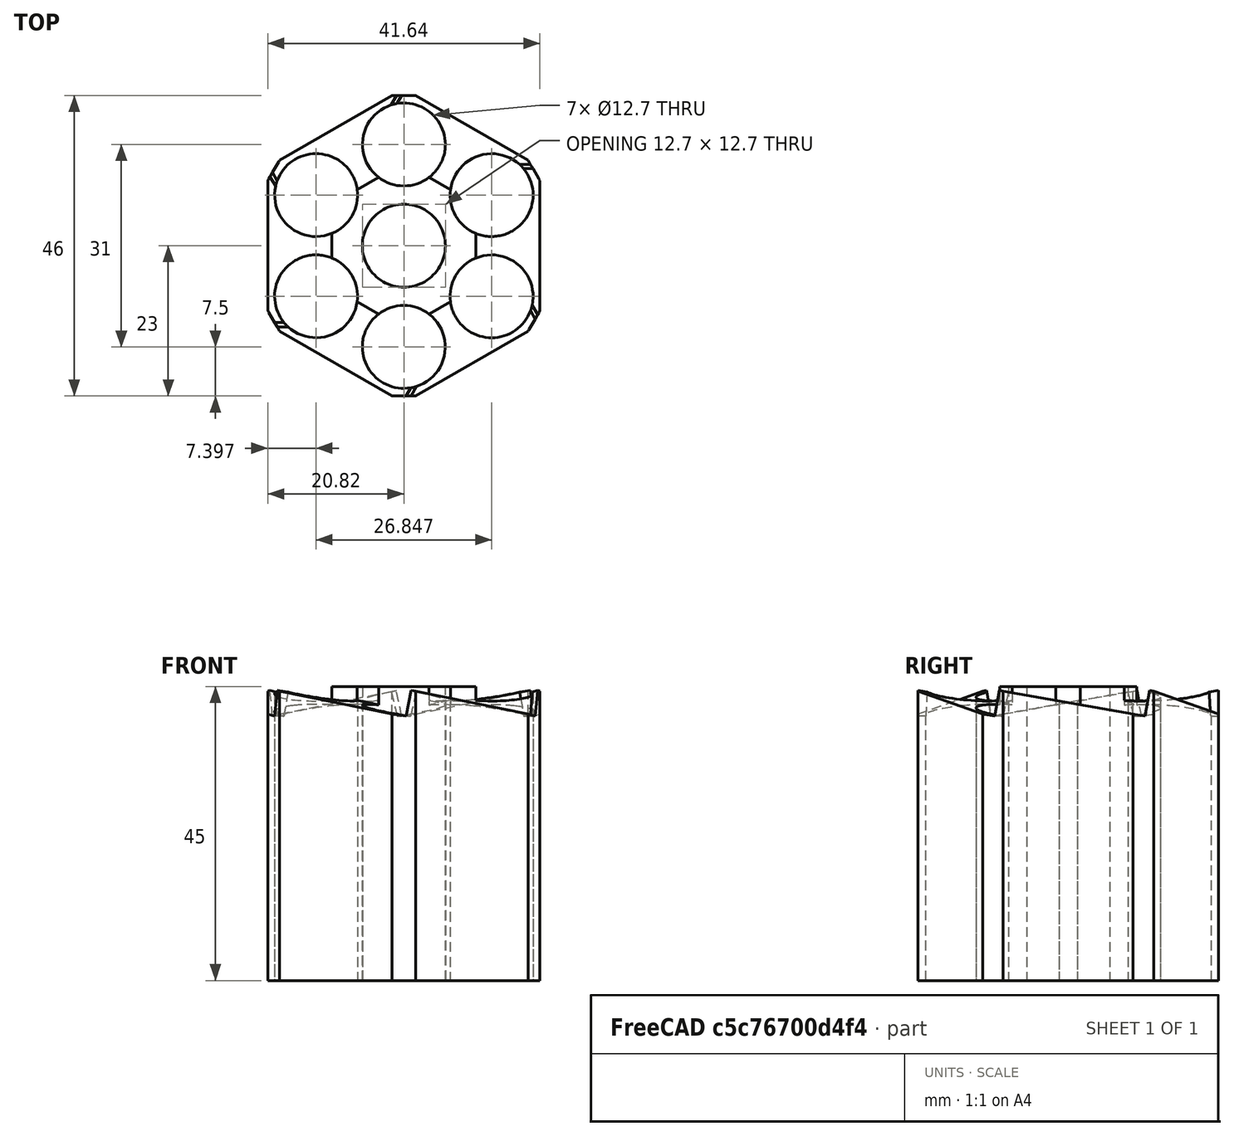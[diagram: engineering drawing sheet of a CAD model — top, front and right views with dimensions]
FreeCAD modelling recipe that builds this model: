
FCSTD DOCUMENT  (FreeCAD 0.20R29410 (Git))
Label: cylinderCore7
License: All rights reserved
LicenseURL: http://en.wikipedia.org/wiki/All_rights_reserved
objects: Part::MultiFuse×108, Part::Box×66, Part::Cylinder×51, Part::Cut×8, Part::Feature×1
note: 234 computed .brp shape members not serialized (recipe doc carries the construction recipe); baked Part::Feature solids carry a one-line shape summary decoded from their .brp

FEATURE [Part::Cylinder] Cylinder
  Angle = 360
  AttacherType = Attacher::AttachEngine3D
  FirstAngle = 0
  Height = 45
  Radius = 25
  SecondAngle = 0
FEATURE [Part::Cylinder] Cylinder001
  Angle = 360
  AttacherType = Attacher::AttachEngine3D
  FirstAngle = 0
  Height = 50
  Placement = pos=(0,15.5,0) rot=(0,0,1;0rad)
  Radius = 6.35
  SecondAngle = 0
FEATURE [Part::Cylinder] Cylinder002
  Angle = 360
  AttacherType = Attacher::AttachEngine3D
  FirstAngle = 0
  Height = 50
  Radius = 6.35
  SecondAngle = 0
FEATURE [Part::Cylinder] Cylinder003  label="bevilPin"
  Angle = 360
  AttacherType = Attacher::AttachEngine3D
  FirstAngle = 0
  Height = 55
  Radius = 6.35
  SecondAngle = 0
FEATURE [Part::MultiFuse] Fusion
  Shapes = -> [Cylinder001,Cylinder002]
FEATURE [Part::Box] Box  label="Cube"
  AttacherType = Attacher::AttachEngine3D
  Height = 50
  Length = 3
  Placement = pos=(-1.5,23,0) rot=(0,0,1;0rad)
  Width = 10
FEATURE [Part::Box] Box001  label="Cube001"
  AttacherType = Attacher::AttachEngine3D
  Height = 50
  Length = 3
  Placement = pos=(12.5753,23,-0.369646) rot=(0,-1,0;0.261799rad)
  Width = 10
FEATURE [Part::Box] Box002  label="Cube002"
  AttacherType = Attacher::AttachEngine3D
  Height = 50
  Length = 3
  Placement = pos=(-1.5,23,0) rot=(0,-1,0;0.523599rad)
  Width = 10
FEATURE [Part::MultiFuse] Fusion001
  Shapes = -> [Box,Box001]
FEATURE [Part::MultiFuse] Fusion002
  Shapes = -> [Fusion001,Box002]
FEATURE [Part::MultiFuse] Fusion003
  Shapes = -> [Fusion,Fusion002]
FEATURE [Part::Box] Box003  label="Cube003"
  AttacherType = Attacher::AttachEngine3D
  Height = 50
  Length = 3
  Placement = pos=(-1.5,23,0) rot=(0,0,1;0rad)
  Width = 10
FEATURE [Part::Box] Box004  label="Cube004"
  AttacherType = Attacher::AttachEngine3D
  Height = 50
  Length = 3
  Placement = pos=(12.5753,23,-0.369646) rot=(0,-1,0;0.261799rad)
  Width = 10
FEATURE [Part::Box] Box005  label="Cube005"
  AttacherType = Attacher::AttachEngine3D
  Height = 50
  Length = 3
  Placement = pos=(-1.5,23,0) rot=(0,-1,0;0.523599rad)
  Width = 10
FEATURE [Part::Cylinder] Cylinder004
  Angle = 360
  AttacherType = Attacher::AttachEngine3D
  FirstAngle = 0
  Height = 50
  Placement = pos=(0,15.5,0) rot=(0,0,1;0rad)
  Radius = 6.35
  SecondAngle = 0
FEATURE [Part::Cylinder] Cylinder005
  Angle = 360
  AttacherType = Attacher::AttachEngine3D
  FirstAngle = 0
  Height = 50
  Radius = 6.35
  SecondAngle = 0
FEATURE [Part::MultiFuse] Fusion004
  Shapes = -> [Cylinder004,Cylinder005]
FEATURE [Part::MultiFuse] Fusion005
  Shapes = -> [Box003,Box004]
FEATURE [Part::MultiFuse] Fusion006
  Shapes = -> [Fusion005,Box005]
FEATURE [Part::MultiFuse] Fusion007
  Placement = pos=(0,0,0) rot=(0,0,1;3.14159rad)
  Shapes = -> [Fusion004,Fusion006]
FEATURE [Part::MultiFuse] Fusion008
  Shapes = -> [Fusion007,Fusion003]
FEATURE [Part::Box] Box006  label="Cube006"
  AttacherType = Attacher::AttachEngine3D
  Height = 50
  Length = 3
  Placement = pos=(-1.5,23,0) rot=(0,0,1;0rad)
  Width = 10
FEATURE [Part::Box] Box007  label="Cube007"
  AttacherType = Attacher::AttachEngine3D
  Height = 50
  Length = 3
  Placement = pos=(12.5753,23,-0.369646) rot=(0,-1,0;0.261799rad)
  Width = 10
FEATURE [Part::Box] Box008  label="Cube008"
  AttacherType = Attacher::AttachEngine3D
  Height = 50
  Length = 3
  Placement = pos=(-1.5,23,0) rot=(0,-1,0;0.523599rad)
  Width = 10
FEATURE [Part::Box] Box009  label="Cube009"
  AttacherType = Attacher::AttachEngine3D
  Height = 50
  Length = 3
  Placement = pos=(-1.5,23,0) rot=(0,0,1;0rad)
  Width = 10
FEATURE [Part::Box] Box010  label="Cube010"
  AttacherType = Attacher::AttachEngine3D
  Height = 50
  Length = 3
  Placement = pos=(12.5753,23,-0.369646) rot=(0,-1,0;0.261799rad)
  Width = 10
FEATURE [Part::Box] Box011  label="Cube011"
  AttacherType = Attacher::AttachEngine3D
  Height = 50
  Length = 3
  Placement = pos=(-1.5,23,0) rot=(0,-1,0;0.523599rad)
  Width = 10
FEATURE [Part::Cylinder] Cylinder006
  Angle = 360
  AttacherType = Attacher::AttachEngine3D
  FirstAngle = 0
  Height = 50
  Placement = pos=(0,15.5,0) rot=(0,0,1;0rad)
  Radius = 6.35
  SecondAngle = 0
FEATURE [Part::Cylinder] Cylinder007
  Angle = 360
  AttacherType = Attacher::AttachEngine3D
  FirstAngle = 0
  Height = 50
  Radius = 6.35
  SecondAngle = 0
FEATURE [Part::Cylinder] Cylinder008
  Angle = 360
  AttacherType = Attacher::AttachEngine3D
  FirstAngle = 0
  Height = 50
  Placement = pos=(0,15.5,0) rot=(0,0,1;0rad)
  Radius = 6.35
  SecondAngle = 0
FEATURE [Part::Cylinder] Cylinder009
  Angle = 360
  AttacherType = Attacher::AttachEngine3D
  FirstAngle = 0
  Height = 50
  Radius = 6.35
  SecondAngle = 0
FEATURE [Part::MultiFuse] Fusion009
  Shapes = -> [Cylinder006,Cylinder007]
FEATURE [Part::MultiFuse] Fusion010
  Shapes = -> [Box006,Box007]
FEATURE [Part::MultiFuse] Fusion011
  Shapes = -> [Fusion010,Box008]
FEATURE [Part::MultiFuse] Fusion012
  Shapes = -> [Fusion009,Fusion011]
FEATURE [Part::MultiFuse] Fusion013
  Shapes = -> [Cylinder008,Cylinder009]
FEATURE [Part::MultiFuse] Fusion014
  Shapes = -> [Box009,Box010]
FEATURE [Part::MultiFuse] Fusion015
  Shapes = -> [Fusion014,Box011]
FEATURE [Part::MultiFuse] Fusion016
  Placement = pos=(0,0,0) rot=(0,0,1;3.14159rad)
  Shapes = -> [Fusion013,Fusion015]
FEATURE [Part::MultiFuse] Fusion017
  Placement = pos=(0,0,0) rot=(0,0,-1;1.0472rad)
  Shapes = -> [Fusion016,Fusion012]
FEATURE [Part::Box] Box012  label="Cube012"
  AttacherType = Attacher::AttachEngine3D
  Height = 50
  Length = 3
  Placement = pos=(-1.5,23,0) rot=(0,0,1;0rad)
  Width = 10
FEATURE [Part::Box] Box013  label="Cube013"
  AttacherType = Attacher::AttachEngine3D
  Height = 50
  Length = 3
  Placement = pos=(12.5753,23,-0.369646) rot=(0,-1,0;0.261799rad)
  Width = 10
FEATURE [Part::Box] Box014  label="Cube014"
  AttacherType = Attacher::AttachEngine3D
  Height = 50
  Length = 3
  Placement = pos=(-1.5,23,0) rot=(0,-1,0;0.523599rad)
  Width = 10
FEATURE [Part::Box] Box015  label="Cube015"
  AttacherType = Attacher::AttachEngine3D
  Height = 50
  Length = 3
  Placement = pos=(-1.5,23,0) rot=(0,0,1;0rad)
  Width = 10
FEATURE [Part::Box] Box016  label="Cube016"
  AttacherType = Attacher::AttachEngine3D
  Height = 50
  Length = 3
  Placement = pos=(12.5753,23,-0.369646) rot=(0,-1,0;0.261799rad)
  Width = 10
FEATURE [Part::Box] Box017  label="Cube017"
  AttacherType = Attacher::AttachEngine3D
  Height = 50
  Length = 3
  Placement = pos=(-1.5,23,0) rot=(0,-1,0;0.523599rad)
  Width = 10
FEATURE [Part::Cylinder] Cylinder010
  Angle = 360
  AttacherType = Attacher::AttachEngine3D
  FirstAngle = 0
  Height = 50
  Placement = pos=(0,15.5,0) rot=(0,0,1;0rad)
  Radius = 6.35
  SecondAngle = 0
FEATURE [Part::Cylinder] Cylinder011
  Angle = 360
  AttacherType = Attacher::AttachEngine3D
  FirstAngle = 0
  Height = 50
  Radius = 6.35
  SecondAngle = 0
FEATURE [Part::Cylinder] Cylinder012
  Angle = 360
  AttacherType = Attacher::AttachEngine3D
  FirstAngle = 0
  Height = 50
  Placement = pos=(0,15.5,0) rot=(0,0,1;0rad)
  Radius = 6.35
  SecondAngle = 0
FEATURE [Part::Cylinder] Cylinder013
  Angle = 360
  AttacherType = Attacher::AttachEngine3D
  FirstAngle = 0
  Height = 50
  Radius = 6.35
  SecondAngle = 0
FEATURE [Part::MultiFuse] Fusion018
  Shapes = -> [Cylinder010,Cylinder011]
FEATURE [Part::MultiFuse] Fusion019
  Shapes = -> [Box012,Box013]
FEATURE [Part::MultiFuse] Fusion020
  Shapes = -> [Fusion019,Box014]
FEATURE [Part::MultiFuse] Fusion021
  Shapes = -> [Fusion018,Fusion020]
FEATURE [Part::MultiFuse] Fusion022
  Shapes = -> [Cylinder012,Cylinder013]
FEATURE [Part::MultiFuse] Fusion023
  Shapes = -> [Box015,Box016]
FEATURE [Part::MultiFuse] Fusion024
  Shapes = -> [Fusion023,Box017]
FEATURE [Part::MultiFuse] Fusion025
  Placement = pos=(0,0,0) rot=(0,0,1;3.14159rad)
  Shapes = -> [Fusion022,Fusion024]
FEATURE [Part::MultiFuse] Fusion026
  Placement = pos=(0,0,0) rot=(0,0,1;4.18879rad)
  Shapes = -> [Fusion025,Fusion021]
FEATURE [Part::MultiFuse] Fusion027
  Shapes = -> [Fusion026,Fusion017]
FEATURE [Part::MultiFuse] Fusion028
  Shapes = -> [Fusion027,Fusion008]
FEATURE [Part::Cut] Cut
  Base = -> Cylinder
  Tool = -> Fusion028
FEATURE [Part::Box] Box018  label="Cube018"
  AttacherType = Attacher::AttachEngine3D
  Height = 50
  Length = 5
  Placement = pos=(-2.5,23,0) rot=(0,0,1;0rad)
  Width = 10
FEATURE [Part::Box] Box019  label="Cube019"
  AttacherType = Attacher::AttachEngine3D
  Height = 55
  Length = 5
  Placement = pos=(-1.23811,24.2566,-4.69879) rot=(0.041494,-0.428539,0.90257;0.912584rad)
  Width = 10
FEATURE [Part::Box] Box020  label="Cube020"
  AttacherType = Attacher::AttachEngine3D
  Height = 10
  Length = 7
  Placement = pos=(-4.5,23,0) rot=(0,0,1;0rad)
  Width = 10
FEATURE [Part::MultiFuse] Fusion029
  Shapes = -> [Box020,Box019]
FEATURE [Part::MultiFuse] Fusion030
  Shapes = -> [Fusion029,Box018]
FEATURE [Part::Cylinder] Cylinder014  label="bevilPin001"
  Angle = 360
  AttacherType = Attacher::AttachEngine3D
  FirstAngle = 0
  Height = 50
  Radius = 6.35
  SecondAngle = 0
FEATURE [Part::MultiFuse] Fusion031
  Shapes = -> [Cylinder014,Fusion030]
FEATURE [Part::Box] Box021  label="Cube021"
  AttacherType = Attacher::AttachEngine3D
  Height = 50
  Length = 5
  Placement = pos=(-2.5,23,0) rot=(0,0,1;0rad)
  Width = 10
FEATURE [Part::Box] Box022  label="Cube022"
  AttacherType = Attacher::AttachEngine3D
  Height = 55
  Length = 5
  Placement = pos=(-1.23811,24.2566,-4.69879) rot=(0.041494,-0.428539,0.90257;0.912584rad)
  Width = 10
FEATURE [Part::Box] Box023  label="Cube023"
  AttacherType = Attacher::AttachEngine3D
  Height = 10
  Length = 7
  Placement = pos=(-4.5,23,0) rot=(0,0,1;0rad)
  Width = 10
FEATURE [Part::Cylinder] Cylinder015  label="bevilPin002"
  Angle = 360
  AttacherType = Attacher::AttachEngine3D
  FirstAngle = 0
  Height = 50
  Radius = 6.35
  SecondAngle = 0
FEATURE [Part::MultiFuse] Fusion032
  Shapes = -> [Box023,Box022]
FEATURE [Part::MultiFuse] Fusion033
  Shapes = -> [Fusion032,Box021]
FEATURE [Part::MultiFuse] Fusion034
  Placement = pos=(0,0,0) rot=(0,0,1;3.14159rad)
  Shapes = -> [Cylinder015,Fusion033]
FEATURE [Part::MultiFuse] Fusion035
  Shapes = -> [Fusion034,Fusion031]
FEATURE [Part::Box] Box024  label="Cube024"
  AttacherType = Attacher::AttachEngine3D
  Height = 50
  Length = 5
  Placement = pos=(-2.5,23,0) rot=(0,0,1;0rad)
  Width = 10
FEATURE [Part::Box] Box025  label="Cube025"
  AttacherType = Attacher::AttachEngine3D
  Height = 55
  Length = 5
  Placement = pos=(-1.23811,24.2566,-4.69879) rot=(0.041494,-0.428539,0.90257;0.912584rad)
  Width = 10
FEATURE [Part::Box] Box026  label="Cube026"
  AttacherType = Attacher::AttachEngine3D
  Height = 10
  Length = 7
  Placement = pos=(-4.5,23,0) rot=(0,0,1;0rad)
  Width = 10
FEATURE [Part::Box] Box027  label="Cube027"
  AttacherType = Attacher::AttachEngine3D
  Height = 50
  Length = 5
  Placement = pos=(-2.5,23,0) rot=(0,0,1;0rad)
  Width = 10
FEATURE [Part::Box] Box028  label="Cube028"
  AttacherType = Attacher::AttachEngine3D
  Height = 55
  Length = 5
  Placement = pos=(-1.23811,24.2566,-4.69879) rot=(0.041494,-0.428539,0.90257;0.912584rad)
  Width = 10
FEATURE [Part::Box] Box029  label="Cube029"
  AttacherType = Attacher::AttachEngine3D
  Height = 10
  Length = 7
  Placement = pos=(-4.5,23,0) rot=(0,0,1;0rad)
  Width = 10
FEATURE [Part::Cylinder] Cylinder016  label="bevilPin003"
  Angle = 360
  AttacherType = Attacher::AttachEngine3D
  FirstAngle = 0
  Height = 50
  Radius = 6.35
  SecondAngle = 0
FEATURE [Part::Cylinder] Cylinder017  label="bevilPin004"
  Angle = 360
  AttacherType = Attacher::AttachEngine3D
  FirstAngle = 0
  Height = 50
  Radius = 6.35
  SecondAngle = 0
FEATURE [Part::MultiFuse] Fusion036
  Shapes = -> [Box026,Box025]
FEATURE [Part::MultiFuse] Fusion037
  Shapes = -> [Fusion036,Box024]
FEATURE [Part::MultiFuse] Fusion038
  Shapes = -> [Cylinder016,Fusion037]
FEATURE [Part::MultiFuse] Fusion039
  Shapes = -> [Box029,Box028]
FEATURE [Part::MultiFuse] Fusion040
  Shapes = -> [Fusion039,Box027]
FEATURE [Part::MultiFuse] Fusion041
  Placement = pos=(0,0,0) rot=(0,0,1;3.14159rad)
  Shapes = -> [Cylinder017,Fusion040]
FEATURE [Part::MultiFuse] Fusion042
  Placement = pos=(0,0,0) rot=(0,0,-1;1.0472rad)
  Shapes = -> [Fusion041,Fusion038]
FEATURE [Part::Box] Box030  label="Cube030"
  AttacherType = Attacher::AttachEngine3D
  Height = 50
  Length = 5
  Placement = pos=(-2.5,23,0) rot=(0,0,1;0rad)
  Width = 10
FEATURE [Part::Box] Box031  label="Cube031"
  AttacherType = Attacher::AttachEngine3D
  Height = 55
  Length = 5
  Placement = pos=(-1.23811,24.2566,-4.69879) rot=(0.041494,-0.428539,0.90257;0.912584rad)
  Width = 10
FEATURE [Part::Box] Box032  label="Cube032"
  AttacherType = Attacher::AttachEngine3D
  Height = 10
  Length = 7
  Placement = pos=(-4.5,23,0) rot=(0,0,1;0rad)
  Width = 10
FEATURE [Part::Box] Box033  label="Cube033"
  AttacherType = Attacher::AttachEngine3D
  Height = 50
  Length = 5
  Placement = pos=(-2.5,23,0) rot=(0,0,1;0rad)
  Width = 10
FEATURE [Part::Box] Box034  label="Cube034"
  AttacherType = Attacher::AttachEngine3D
  Height = 55
  Length = 5
  Placement = pos=(-1.23811,24.2566,-4.69879) rot=(0.041494,-0.428539,0.90257;0.912584rad)
  Width = 10
FEATURE [Part::Box] Box035  label="Cube035"
  AttacherType = Attacher::AttachEngine3D
  Height = 10
  Length = 7
  Placement = pos=(-4.5,23,0) rot=(0,0,1;0rad)
  Width = 10
FEATURE [Part::Cylinder] Cylinder018  label="bevilPin005"
  Angle = 360
  AttacherType = Attacher::AttachEngine3D
  FirstAngle = 0
  Height = 50
  Radius = 6.35
  SecondAngle = 0
FEATURE [Part::Cylinder] Cylinder019  label="bevilPin006"
  Angle = 360
  AttacherType = Attacher::AttachEngine3D
  FirstAngle = 0
  Height = 50
  Radius = 6.35
  SecondAngle = 0
FEATURE [Part::MultiFuse] Fusion043
  Shapes = -> [Box032,Box031]
FEATURE [Part::MultiFuse] Fusion044
  Shapes = -> [Fusion043,Box030]
FEATURE [Part::MultiFuse] Fusion045
  Shapes = -> [Cylinder018,Fusion044]
FEATURE [Part::MultiFuse] Fusion046
  Shapes = -> [Box035,Box034]
FEATURE [Part::MultiFuse] Fusion047
  Shapes = -> [Fusion046,Box033]
FEATURE [Part::MultiFuse] Fusion048
  Placement = pos=(0,0,0) rot=(0,0,1;3.14159rad)
  Shapes = -> [Cylinder019,Fusion047]
FEATURE [Part::MultiFuse] Fusion049
  Placement = pos=(0,0,0) rot=(0,0,1;4.18879rad)
  Shapes = -> [Fusion048,Fusion045]
FEATURE [Part::MultiFuse] Fusion050
  Shapes = -> [Fusion049,Fusion042]
FEATURE [Part::MultiFuse] Fusion051
  Shapes = -> [Fusion050,Fusion035]
FEATURE [Part::Cut] Cut001
  Base = -> Cut
  Tool = -> Fusion051
FEATURE [Part::Box] Box036  label="Cube036"
  AttacherType = Attacher::AttachEngine3D
  Height = 50
  Length = 7
  Placement = pos=(0.388229,23.9489,0) rot=(0,0,-1;0.261799rad)
  Width = 7
FEATURE [Part::Cylinder] Cylinder020  label="bevilPin007"
  Angle = 360
  AttacherType = Attacher::AttachEngine3D
  FirstAngle = 0
  Height = 50
  Radius = 6.35
  SecondAngle = 0
FEATURE [Part::MultiFuse] Fusion052
  Shapes = -> [Cylinder020,Box036]
FEATURE [Part::Box] Box037  label="Cube037"
  AttacherType = Attacher::AttachEngine3D
  Height = 50
  Length = 7
  Placement = pos=(0.388229,23.9489,0) rot=(0,0,-1;0.261799rad)
  Width = 7
FEATURE [Part::Cylinder] Cylinder021  label="bevilPin008"
  Angle = 360
  AttacherType = Attacher::AttachEngine3D
  FirstAngle = 0
  Height = 50
  Radius = 6.35
  SecondAngle = 0
FEATURE [Part::MultiFuse] Fusion053
  Placement = pos=(0,0,0) rot=(0,0,1;3.14159rad)
  Shapes = -> [Cylinder021,Box037]
FEATURE [Part::MultiFuse] Fusion054
  Shapes = -> [Fusion053,Fusion052]
FEATURE [Part::Box] Box038  label="Cube038"
  AttacherType = Attacher::AttachEngine3D
  Height = 50
  Length = 7
  Placement = pos=(0.388229,23.9489,0) rot=(0,0,-1;0.261799rad)
  Width = 7
FEATURE [Part::Box] Box039  label="Cube039"
  AttacherType = Attacher::AttachEngine3D
  Height = 50
  Length = 7
  Placement = pos=(0.388229,23.9489,0) rot=(0,0,-1;0.261799rad)
  Width = 7
FEATURE [Part::Cylinder] Cylinder022  label="bevilPin009"
  Angle = 360
  AttacherType = Attacher::AttachEngine3D
  FirstAngle = 0
  Height = 50
  Radius = 6.35
  SecondAngle = 0
FEATURE [Part::Cylinder] Cylinder023  label="bevilPin010"
  Angle = 360
  AttacherType = Attacher::AttachEngine3D
  FirstAngle = 0
  Height = 50
  Radius = 6.35
  SecondAngle = 0
FEATURE [Part::MultiFuse] Fusion055
  Shapes = -> [Cylinder022,Box038]
FEATURE [Part::MultiFuse] Fusion056
  Placement = pos=(0,0,0) rot=(0,0,1;3.14159rad)
  Shapes = -> [Cylinder023,Box039]
FEATURE [Part::MultiFuse] Fusion057
  Placement = pos=(0,0,0) rot=(0,0,-1;1.0472rad)
  Shapes = -> [Fusion056,Fusion055]
FEATURE [Part::Box] Box040  label="Cube040"
  AttacherType = Attacher::AttachEngine3D
  Height = 50
  Length = 7
  Placement = pos=(0.388229,23.9489,0) rot=(0,0,-1;0.261799rad)
  Width = 7
FEATURE [Part::Box] Box041  label="Cube041"
  AttacherType = Attacher::AttachEngine3D
  Height = 50
  Length = 7
  Placement = pos=(0.388229,23.9489,0) rot=(0,0,-1;0.261799rad)
  Width = 7
FEATURE [Part::Cylinder] Cylinder024  label="bevilPin011"
  Angle = 360
  AttacherType = Attacher::AttachEngine3D
  FirstAngle = 0
  Height = 50
  Radius = 6.35
  SecondAngle = 0
FEATURE [Part::Cylinder] Cylinder025  label="bevilPin012"
  Angle = 360
  AttacherType = Attacher::AttachEngine3D
  FirstAngle = 0
  Height = 50
  Radius = 6.35
  SecondAngle = 0
FEATURE [Part::MultiFuse] Fusion058
  Shapes = -> [Cylinder024,Box040]
FEATURE [Part::MultiFuse] Fusion059
  Placement = pos=(0,0,0) rot=(0,0,1;3.14159rad)
  Shapes = -> [Cylinder025,Box041]
FEATURE [Part::MultiFuse] Fusion060
  Placement = pos=(0,0,0) rot=(0,0,1;1.0472rad)
  Shapes = -> [Fusion059,Fusion058]
FEATURE [Part::MultiFuse] Fusion061
  Shapes = -> [Fusion060,Fusion057]
FEATURE [Part::MultiFuse] Fusion062
  Shapes = -> [Fusion061,Fusion054]
FEATURE [Part::Cut] Cut002
  Base = -> Cut001
  Tool = -> Fusion062
FEATURE [Part::Cylinder] Cylinder026  label="bevilPin013"
  Angle = 360
  AttacherType = Attacher::AttachEngine3D
  FirstAngle = 0
  Height = 50
  Radius = 6.35
  SecondAngle = 0
FEATURE [Part::Box] Box042  label="Cube042"
  AttacherType = Attacher::AttachEngine3D
  Height = 50
  Length = 6
  Placement = pos=(-3.33531,23,-4.34667) rot=(0,-1,0;0.261799rad)
  Width = 10
FEATURE [Part::MultiFuse] Fusion063
  Shapes = -> [Cylinder026,Box042]
FEATURE [Part::Box] Box043  label="Cube043"
  AttacherType = Attacher::AttachEngine3D
  Height = 50
  Length = 6
  Placement = pos=(-3.33531,23,-4.34667) rot=(0,-1,0;0.261799rad)
  Width = 10
FEATURE [Part::Cylinder] Cylinder027  label="bevilPin014"
  Angle = 360
  AttacherType = Attacher::AttachEngine3D
  FirstAngle = 0
  Height = 50
  Radius = 6.35
  SecondAngle = 0
FEATURE [Part::MultiFuse] Fusion064
  Placement = pos=(0,0,0) rot=(0,0,1;3.14159rad)
  Shapes = -> [Cylinder027,Box043]
FEATURE [Part::MultiFuse] Fusion065
  Shapes = -> [Fusion064,Fusion063]
FEATURE [Part::Box] Box044  label="Cube044"
  AttacherType = Attacher::AttachEngine3D
  Height = 50
  Length = 6
  Placement = pos=(-3.33531,23,-4.34667) rot=(0,-1,0;0.261799rad)
  Width = 10
FEATURE [Part::Box] Box045  label="Cube045"
  AttacherType = Attacher::AttachEngine3D
  Height = 50
  Length = 6
  Placement = pos=(-3.33531,23,-4.34667) rot=(0,-1,0;0.261799rad)
  Width = 10
FEATURE [Part::Cylinder] Cylinder028  label="bevilPin015"
  Angle = 360
  AttacherType = Attacher::AttachEngine3D
  FirstAngle = 0
  Height = 50
  Radius = 6.35
  SecondAngle = 0
FEATURE [Part::Cylinder] Cylinder029  label="bevilPin016"
  Angle = 360
  AttacherType = Attacher::AttachEngine3D
  FirstAngle = 0
  Height = 50
  Radius = 6.35
  SecondAngle = 0
FEATURE [Part::MultiFuse] Fusion066
  Shapes = -> [Cylinder028,Box044]
FEATURE [Part::MultiFuse] Fusion067
  Placement = pos=(0,0,0) rot=(0,0,1;3.14159rad)
  Shapes = -> [Cylinder029,Box045]
FEATURE [Part::MultiFuse] Fusion068
  Placement = pos=(0,0,0) rot=(0,0,1;1.0472rad)
  Shapes = -> [Fusion067,Fusion066]
FEATURE [Part::Box] Box046  label="Cube046"
  AttacherType = Attacher::AttachEngine3D
  Height = 50
  Length = 6
  Placement = pos=(-3.33531,23,-4.34667) rot=(0,-1,0;0.261799rad)
  Width = 10
FEATURE [Part::Box] Box047  label="Cube047"
  AttacherType = Attacher::AttachEngine3D
  Height = 50
  Length = 6
  Placement = pos=(-3.33531,23,-4.34667) rot=(0,-1,0;0.261799rad)
  Width = 10
FEATURE [Part::Cylinder] Cylinder030  label="bevilPin017"
  Angle = 360
  AttacherType = Attacher::AttachEngine3D
  FirstAngle = 0
  Height = 50
  Radius = 6.35
  SecondAngle = 0
FEATURE [Part::Cylinder] Cylinder031  label="bevilPin018"
  Angle = 360
  AttacherType = Attacher::AttachEngine3D
  FirstAngle = 0
  Height = 50
  Radius = 6.35
  SecondAngle = 0
FEATURE [Part::MultiFuse] Fusion069
  Shapes = -> [Cylinder030,Box046]
FEATURE [Part::MultiFuse] Fusion070
  Placement = pos=(0,0,0) rot=(0,0,1;3.14159rad)
  Shapes = -> [Cylinder031,Box047]
FEATURE [Part::MultiFuse] Fusion071
  Placement = pos=(0,0,0) rot=(0,0,1;2.0944rad)
  Shapes = -> [Fusion070,Fusion069]
FEATURE [Part::MultiFuse] Fusion072
  Shapes = -> [Fusion065,Fusion068]
FEATURE [Part::MultiFuse] Fusion073
  Shapes = -> [Fusion072,Fusion071]
FEATURE [Part::Cut] Cut003
  Base = -> Cut002
  Tool = -> Fusion073
FEATURE [Part::Cylinder] Cylinder032  label="bevilPin019"
  Angle = 360
  AttacherType = Attacher::AttachEngine3D
  FirstAngle = 0
  Height = 50
  Radius = 6.35
  SecondAngle = 0
FEATURE [Part::Box] Box048  label="Cube048"
  AttacherType = Attacher::AttachEngine3D
  Height = 10
  Length = 19
  Placement = pos=(10.1338,22.4017,35.5) rot=(0,0,-1;0.785398rad)
  Width = 3
FEATURE [Part::MultiFuse] Fusion074
  Shapes = -> [Box048,Cylinder032]
FEATURE [Part::Cylinder] Cylinder033  label="bevilPin020"
  Angle = 360
  AttacherType = Attacher::AttachEngine3D
  FirstAngle = 0
  Height = 50
  Radius = 6.35
  SecondAngle = 0
FEATURE [Part::Box] Box049  label="Cube049"
  AttacherType = Attacher::AttachEngine3D
  Height = 10
  Length = 19
  Placement = pos=(10.1338,22.4017,35.5) rot=(0,0,-1;0.785398rad)
  Width = 3
FEATURE [Part::MultiFuse] Fusion075
  Placement = pos=(0,0,0) rot=(0,0,1;3.14159rad)
  Shapes = -> [Box049,Cylinder033]
FEATURE [Part::MultiFuse] Fusion076
  Shapes = -> [Fusion074,Fusion075]
FEATURE [Part::Box] Box050  label="Cube050"
  AttacherType = Attacher::AttachEngine3D
  Height = 10
  Length = 19
  Placement = pos=(10.1338,22.4017,35.5) rot=(0,0,-1;0.785398rad)
  Width = 3
FEATURE [Part::Cylinder] Cylinder034  label="bevilPin021"
  Angle = 360
  AttacherType = Attacher::AttachEngine3D
  FirstAngle = 0
  Height = 50
  Radius = 6.35
  SecondAngle = 0
FEATURE [Part::MultiFuse] Fusion077
  Placement = pos=(0,0,0) rot=(0,0,1;3.14159rad)
  Shapes = -> [Box050,Cylinder034]
FEATURE [Part::Cylinder] Cylinder035  label="bevilPin022"
  Angle = 360
  AttacherType = Attacher::AttachEngine3D
  FirstAngle = 0
  Height = 50
  Radius = 6.35
  SecondAngle = 0
FEATURE [Part::Box] Box051  label="Cube051"
  AttacherType = Attacher::AttachEngine3D
  Height = 10
  Length = 19
  Placement = pos=(10.1338,22.4017,35.5) rot=(0,0,-1;0.785398rad)
  Width = 3
FEATURE [Part::MultiFuse] Fusion079
  Shapes = -> [Box051,Cylinder035]
FEATURE [Part::MultiFuse] Fusion078
  Placement = pos=(0,0,0) rot=(0,0,-1;1.0472rad)
  Shapes = -> [Fusion079,Fusion077]
FEATURE [Part::Box] Box052  label="Cube052"
  AttacherType = Attacher::AttachEngine3D
  Height = 10
  Length = 19
  Placement = pos=(10.1338,22.4017,35.5) rot=(0,0,-1;0.785398rad)
  Width = 3
FEATURE [Part::Cylinder] Cylinder036  label="bevilPin023"
  Angle = 360
  AttacherType = Attacher::AttachEngine3D
  FirstAngle = 0
  Height = 50
  Radius = 6.35
  SecondAngle = 0
FEATURE [Part::Box] Box053  label="Cube053"
  AttacherType = Attacher::AttachEngine3D
  Height = 10
  Length = 19
  Placement = pos=(10.1338,22.4017,35.5) rot=(0,0,-1;0.785398rad)
  Width = 3
FEATURE [Part::Cylinder] Cylinder037  label="bevilPin024"
  Angle = 360
  AttacherType = Attacher::AttachEngine3D
  FirstAngle = 0
  Height = 50
  Radius = 6.35
  SecondAngle = 0
FEATURE [Part::MultiFuse] Fusion080
  Placement = pos=(0,0,0) rot=(0,0,1;3.14159rad)
  Shapes = -> [Box052,Cylinder037]
FEATURE [Part::MultiFuse] Fusion081
  Shapes = -> [Box053,Cylinder036]
FEATURE [Part::MultiFuse] Fusion082
  Placement = pos=(0,0,0) rot=(0,0,1;4.18879rad)
  Shapes = -> [Fusion081,Fusion080]
FEATURE [Part::MultiFuse] Fusion083
  Shapes = -> [Fusion078,Fusion082]
FEATURE [Part::MultiFuse] Fusion084
  Shapes = -> [Fusion083,Fusion076]
FEATURE [Part::Cut] Cut004
  Base = -> Cut003
  Tool = -> Fusion084
FEATURE [Part::Box] Box059  label="Cube059"
  AttacherType = Attacher::AttachEngine3D
  Height = 50
  Length = 31
  Placement = pos=(-2.14505,25.2794,-2.5) rot=(0,0,-1;0.523599rad)
  Width = 6
FEATURE [Part::Cylinder] Cylinder042  label="bevilPin029"
  Angle = 360
  AttacherType = Attacher::AttachEngine3D
  FirstAngle = 0
  Height = 50
  Radius = 6.35
  SecondAngle = 0
FEATURE [Part::MultiFuse] Fusion085
  Shapes = -> [Box059,Cylinder042]
FEATURE [Part::Box] Box060  label="Cube060"
  AttacherType = Attacher::AttachEngine3D
  Height = 50
  Length = 31
  Placement = pos=(-2.14505,25.2794,-2.5) rot=(0,0,-1;0.523599rad)
  Width = 6
FEATURE [Part::Cylinder] Cylinder043  label="bevilPin030"
  Angle = 360
  AttacherType = Attacher::AttachEngine3D
  FirstAngle = 0
  Height = 50
  Radius = 6.35
  SecondAngle = 0
FEATURE [Part::MultiFuse] Fusion086
  Placement = pos=(0,0,0) rot=(0,0,1;3.14159rad)
  Shapes = -> [Box060,Cylinder043]
FEATURE [Part::MultiFuse] Fusion087
  Shapes = -> [Fusion086,Fusion085]
FEATURE [Part::Box] Box061  label="Cube061"
  AttacherType = Attacher::AttachEngine3D
  Height = 50
  Length = 31
  Placement = pos=(-2.14505,25.2794,-2.5) rot=(0,0,-1;0.523599rad)
  Width = 6
FEATURE [Part::Cylinder] Cylinder044  label="bevilPin031"
  Angle = 360
  AttacherType = Attacher::AttachEngine3D
  FirstAngle = 0
  Height = 50
  Radius = 6.35
  SecondAngle = 0
FEATURE [Part::Box] Box062  label="Cube062"
  AttacherType = Attacher::AttachEngine3D
  Height = 50
  Length = 31
  Placement = pos=(-2.14505,25.2794,-2.5) rot=(0,0,-1;0.523599rad)
  Width = 6
FEATURE [Part::Cylinder] Cylinder045  label="bevilPin032"
  Angle = 360
  AttacherType = Attacher::AttachEngine3D
  FirstAngle = 0
  Height = 50
  Radius = 6.35
  SecondAngle = 0
FEATURE [Part::MultiFuse] Fusion088
  Placement = pos=(0,0,0) rot=(0,0,1;3.14159rad)
  Shapes = -> [Box061,Cylinder044]
FEATURE [Part::MultiFuse] Fusion089
  Shapes = -> [Box062,Cylinder045]
FEATURE [Part::MultiFuse] Fusion090
  Placement = pos=(0,0,0) rot=(0,0,-1;1.0472rad)
  Shapes = -> [Fusion088,Fusion089]
FEATURE [Part::Box] Box063  label="Cube063"
  AttacherType = Attacher::AttachEngine3D
  Height = 50
  Length = 31
  Placement = pos=(-2.14505,25.2794,-2.5) rot=(0,0,-1;0.523599rad)
  Width = 6
FEATURE [Part::Cylinder] Cylinder046  label="bevilPin033"
  Angle = 360
  AttacherType = Attacher::AttachEngine3D
  FirstAngle = 0
  Height = 50
  Radius = 6.35
  SecondAngle = 0
FEATURE [Part::Box] Box064  label="Cube064"
  AttacherType = Attacher::AttachEngine3D
  Height = 50
  Length = 31
  Placement = pos=(-2.14505,25.2794,-2.5) rot=(0,0,-1;0.523599rad)
  Width = 6
FEATURE [Part::Cylinder] Cylinder047  label="bevilPin034"
  Angle = 360
  AttacherType = Attacher::AttachEngine3D
  FirstAngle = 0
  Height = 50
  Radius = 6.35
  SecondAngle = 0
FEATURE [Part::MultiFuse] Fusion091
  Placement = pos=(0,0,0) rot=(0,0,1;3.14159rad)
  Shapes = -> [Box063,Cylinder046]
FEATURE [Part::MultiFuse] Fusion092
  Shapes = -> [Box064,Cylinder047]
FEATURE [Part::MultiFuse] Fusion093
  Placement = pos=(0,0,0) rot=(0,0,-1;2.0944rad)
  Shapes = -> [Fusion091,Fusion092]
FEATURE [Part::MultiFuse] Fusion094
  Shapes = -> [Fusion093,Fusion090]
FEATURE [Part::MultiFuse] Fusion095
  Shapes = -> [Fusion094,Fusion087]
FEATURE [Part::Cut] Cut005
  Base = -> Cut004
  Tool = -> Fusion095
FEATURE [Part::Cylinder] Cylinder048  label="bevilPin035"
  Angle = 360
  AttacherType = Attacher::AttachEngine3D
  FirstAngle = 0
  Height = 55
  Radius = 6.35
  SecondAngle = 0
FEATURE [Part::Box] Box065  label="Cube065"
  AttacherType = Attacher::AttachEngine3D
  Height = 20
  Length = 10
  Placement = pos=(11,-12.8391,44.8084) rot=(-1,0,0;0.174533rad)
  Width = 25
FEATURE [Part::MultiFuse] Fusion096
  Shapes = -> [Cylinder048,Box065]
FEATURE [Part::Cylinder] Cylinder049  label="bevilPin036"
  Angle = 360
  AttacherType = Attacher::AttachEngine3D
  FirstAngle = 0
  Height = 55
  Radius = 6.35
  SecondAngle = 0
FEATURE [Part::Box] Box066  label="Cube066"
  AttacherType = Attacher::AttachEngine3D
  Height = 20
  Length = 10
  Placement = pos=(11,-12.8391,44.8084) rot=(-1,0,0;0.174533rad)
  Width = 25
FEATURE [Part::MultiFuse] Fusion097
  Placement = pos=(0,0,0) rot=(0,0,1;3.14159rad)
  Shapes = -> [Cylinder049,Box066]
FEATURE [Part::MultiFuse] Fusion098
  Shapes = -> [Fusion096,Fusion097]
FEATURE [Part::Cylinder] Cylinder050  label="bevilPin037"
  Angle = 360
  AttacherType = Attacher::AttachEngine3D
  FirstAngle = 0
  Height = 55
  Radius = 6.35
  SecondAngle = 0
FEATURE [Part::Cylinder] Cylinder051  label="bevilPin038"
  Angle = 360
  AttacherType = Attacher::AttachEngine3D
  FirstAngle = 0
  Height = 55
  Radius = 6.35
  SecondAngle = 0
FEATURE [Part::Box] Box067  label="Cube067"
  AttacherType = Attacher::AttachEngine3D
  Height = 20
  Length = 10
  Placement = pos=(11,-12.8391,44.8084) rot=(-1,0,0;0.174533rad)
  Width = 25
FEATURE [Part::Box] Box068  label="Cube068"
  AttacherType = Attacher::AttachEngine3D
  Height = 20
  Length = 10
  Placement = pos=(11,-12.8391,44.8084) rot=(-1,0,0;0.174533rad)
  Width = 25
FEATURE [Part::MultiFuse] Fusion099
  Placement = pos=(0,0,0) rot=(0,0,1;3.14159rad)
  Shapes = -> [Cylinder050,Box068]
FEATURE [Part::MultiFuse] Fusion100
  Shapes = -> [Cylinder051,Box067]
FEATURE [Part::MultiFuse] Fusion101
  Placement = pos=(0,0,0) rot=(0,0,-1;1.0472rad)
  Shapes = -> [Fusion100,Fusion099]
FEATURE [Part::Cylinder] Cylinder052  label="bevilPin039"
  Angle = 360
  AttacherType = Attacher::AttachEngine3D
  FirstAngle = 0
  Height = 55
  Radius = 6.35
  SecondAngle = 0
FEATURE [Part::Cylinder] Cylinder053  label="bevilPin040"
  Angle = 360
  AttacherType = Attacher::AttachEngine3D
  FirstAngle = 0
  Height = 55
  Radius = 6.35
  SecondAngle = 0
FEATURE [Part::Box] Box069  label="Cube069"
  AttacherType = Attacher::AttachEngine3D
  Height = 20
  Length = 10
  Placement = pos=(11,-12.8391,44.8084) rot=(-1,0,0;0.174533rad)
  Width = 25
FEATURE [Part::Box] Box070  label="Cube070"
  AttacherType = Attacher::AttachEngine3D
  Height = 20
  Length = 10
  Placement = pos=(11,-12.8391,44.8084) rot=(-1,0,0;0.174533rad)
  Width = 25
FEATURE [Part::MultiFuse] Fusion102
  Placement = pos=(0,0,0) rot=(0,0,1;3.14159rad)
  Shapes = -> [Cylinder052,Box070]
FEATURE [Part::MultiFuse] Fusion103
  Shapes = -> [Cylinder053,Box069]
FEATURE [Part::MultiFuse] Fusion104
  Placement = pos=(0,0,0) rot=(0,0,-1;2.0944rad)
  Shapes = -> [Fusion103,Fusion102]
FEATURE [Part::MultiFuse] Fusion105
  Shapes = -> [Fusion104,Fusion101]
FEATURE [Part::MultiFuse] Fusion106
  Shapes = -> [Fusion105,Fusion098]
FEATURE [Part::Cut] Cut006
  Base = -> Cut005
  Tool = -> Fusion106
FEATURE [Part::MultiFuse] Fusion107
  Shapes = -> [Cylinder003,Cut006]
FEATURE [Part::Cylinder] Cylinder054
  Angle = 360
  AttacherType = Attacher::AttachEngine3D
  FirstAngle = 0
  Height = 55
  Radius = 6.35
  SecondAngle = 0
FEATURE [Part::Cut] Cut007
  Base = -> Fusion107
  Tool = -> Cylinder054
FEATURE [Part::Feature] Cut007_solid  label="Cut007 (Solid)"
  shape: bbox 41.64 x 46 x 45 mm, 117 faces (baked)
